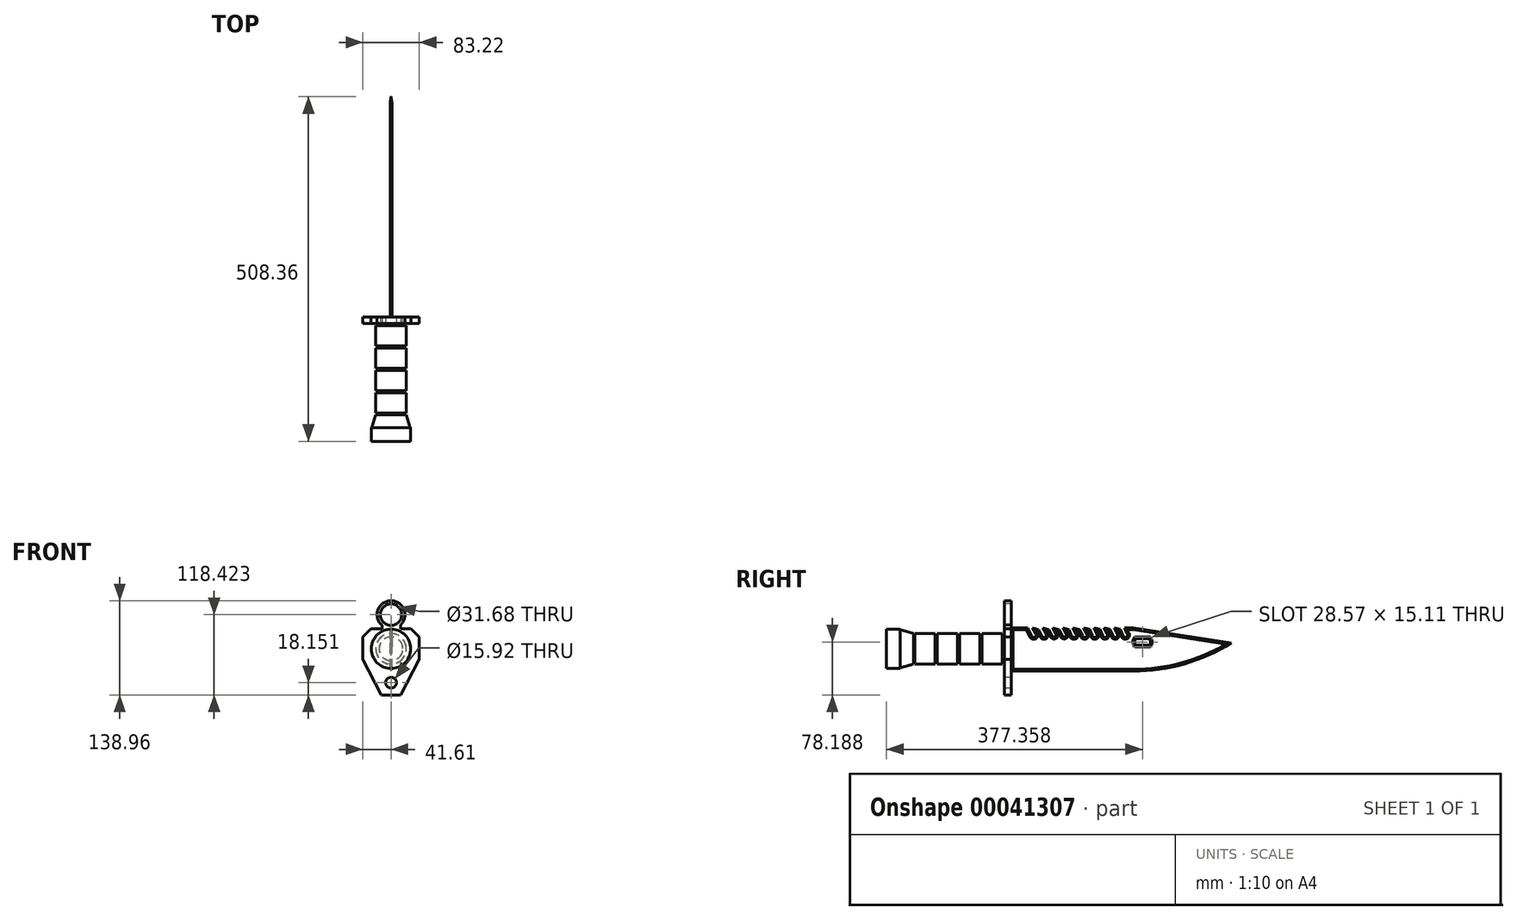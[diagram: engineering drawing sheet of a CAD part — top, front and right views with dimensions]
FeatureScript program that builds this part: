
annotation { "Feature Type Name" : "Feature", "Feature Type Description" : "" }
export const myFeature = defineFeature(function(context is Context, id is Id, definition is map)
    precondition{}
    {
        {
            var Q0;
            Q0=qCreatedBy(makeId("Right.planeOp"),FACE);
            var sketch = newSketch(context, id + "F0", { "sketchPlane" : qUnion([Q0])});
            skLineSegment(sketch, "E0", {"start": v(0, 0) * mm, "end": v(0, 17.36) * mm});
            skLineSegment(sketch, "E1", {"start": v(0, 17.36) * mm, "end": v(-3, 17.36) * mm});
            skLineSegment(sketch, "E2", {"start": v(-3, 17.36) * mm, "end": v(-3, 22.36) * mm});
            skLineSegment(sketch, "E3", {"start": v(-3, 22.36) * mm, "end": v(-33, 22.36) * mm});
            skLineSegment(sketch, "E4", {"start": v(-33, 22.36) * mm, "end": v(-33, 17.36) * mm});
            skLineSegment(sketch, "E5", {"start": v(-33, 17.36) * mm, "end": v(-36, 17.36) * mm});
            skLineSegment(sketch, "E6", {"start": v(-36, 17.36) * mm, "end": v(-36, 22.36) * mm});
            skLineSegment(sketch, "E7", {"start": v(-36, 22.36) * mm, "end": v(-66, 22.36) * mm});
            skLineSegment(sketch, "E8", {"start": v(-66, 22.36) * mm, "end": v(-66, 17.36) * mm});
            skLineSegment(sketch, "E9", {"start": v(-66, 17.36) * mm, "end": v(-69, 17.36) * mm});
            skLineSegment(sketch, "E10", {"start": v(-69, 17.36) * mm, "end": v(-69, 22.36) * mm});
            skLineSegment(sketch, "E11", {"start": v(-69, 22.36) * mm, "end": v(-99, 22.36) * mm});
            skLineSegment(sketch, "E12", {"start": v(-99, 22.36) * mm, "end": v(-99, 17.36) * mm});
            skLineSegment(sketch, "E13", {"start": v(-99, 17.36) * mm, "end": v(-102, 17.36) * mm});
            skLineSegment(sketch, "E14", {"start": v(-102, 17.36) * mm, "end": v(-102, 22.36) * mm});
            skLineSegment(sketch, "E15", {"start": v(-102, 22.36) * mm, "end": v(-132, 22.36) * mm});
            skLineSegment(sketch, "E16", {"start": v(-132, 22.36) * mm, "end": v(-132, 17.64) * mm});
            skLineSegment(sketch, "E17", {"start": v(-132, 17.64) * mm, "end": v(-134, 17.64) * mm});
            skLineSegment(sketch, "E18", {"start": v(-134, 17.64) * mm, "end": v(-134, 22.64) * mm});
            skLineSegment(sketch, "E19", {"start": v(-134, 22.64) * mm, "end": v(-153.56, 28.06) * mm});
            skLineSegment(sketch, "E20", {"start": v(-153.56, 28.06) * mm, "end": v(-153.56, 29.06) * mm});
            skLineSegment(sketch, "E21", {"start": v(-153.56, 29.06) * mm, "end": v(-173.56, 29.06) * mm});
            skLineSegment(sketch, "E22", {"start": v(-173.56, 29.06) * mm, "end": v(-173.56, 0) * mm});
            skLineSegment(sketch, "E23", {"start": v(-173.56, 0) * mm, "end": v(0, 0) * mm});
            skSolve(sketch);
        }
        {
            var Q0;
            Q0 = qSketchRegion(id + "F0", true);
            var Q1;
            Q1=sQuery(id+"F0.wireOp",EDGE,"E23");
            revolve(context, id + "F1", {"entities" : qUnion([Q0]), "axis" : qUnion([Q1]), "revolveType" : RevolveType.FULL});
        }
        {
            var Q0;
            Q0=qCreatedBy(makeId("Front.planeOp"),FACE);
            var sketch = newSketch(context, id + "F2", { "sketchPlane" : qUnion([Q0])});
            skLineSegment(sketch, "E24", {"start": v(0, -68.1) * mm, "end": v(14.11, -68.1) * mm});
            skLineSegment(sketch, "E25", {"start": v(14.11, -68.1) * mm, "end": v(41.6, -15.3) * mm});
            skLineSegment(sketch, "E26", {"start": v(41.6, -15.3) * mm, "end": v(41.6, 17.5) * mm});
            skLineSegment(sketch, "E27", {"start": v(0, 29.79) * mm, "end": v(29.7, 29.79) * mm});
            skLineSegment(sketch, "E28", {"start": v(29.7, 29.79) * mm, "end": v(41.6, 17.5) * mm});
            skLineSegment(sketch, "E29.MirrorCS", {"start": v(-41.6, -15.3) * mm, "end": v(-41.6, 17.5) * mm});
            skLineSegment(sketch, "E30.MirrorCS", {"start": v(0, 29.79) * mm, "end": v(-29.7, 29.79) * mm});
            skLineSegment(sketch, "E31.MirrorCS", {"start": v(0, -68.1) * mm, "end": v(-14.11, -68.1) * mm});
            skLineSegment(sketch, "E32.MirrorCS", {"start": v(-14.11, -68.1) * mm, "end": v(-41.6, -15.3) * mm});
            skLineSegment(sketch, "E33.MirrorCS", {"start": v(-29.7, 29.79) * mm, "end": v(-41.6, 17.5) * mm});
            skCircle(sketch, "E34", {"center": v(0, -49.95) * mm, "radius": 7.96 * mm});
            skCircle(sketch, "E35", {"center": v(0, 50.32) * mm, "radius": 20.54 * mm});
            skCircle(sketch, "E36", {"center": v(0, 50.32) * mm, "radius": 15.84 * mm});
            skLineSegment(sketch, "E37", {"start": v(14.21, 35.5) * mm, "end": v(14.21, 29.79) * mm});
            skLineSegment(sketch, "E38", {"start": v(-13.2, 29.79) * mm, "end": v(-13.2, 34.59) * mm});
            skSolve(sketch);
        }
        {
            var Q0;
            Q0 = qSketchRegion(id + "F2", true);
            extrude(context, id + "F3", {"entities" : qUnion([Q0]), "operationType" : NewBodyOperationType.ADD, "oppositeDirection" : true, "depth" : 10 * mm});
        }
        {
            var Q0;
            Q0=qCreatedBy(makeId("Right.planeOp"),FACE);
            var sketch = newSketch(context, id + "F4", { "sketchPlane" : qUnion([Q0])});
            skLineSegment(sketch, "E39", {"start": v(0, 0) * mm, "end": v(0, 30.7) * mm});
            skLineSegment(sketch, "E40", {"start": v(10.33, 30.7) * mm, "end": v(190.33, 30.7) * mm});
            skLineSegment(sketch, "E41", {"start": v(190.33, 30.7) * mm, "end": v(334.8, 8.42) * mm});
            skLineSegment(sketch, "E42", {"start": v(10.33, -32.89) * mm, "end": v(190.33, -32.89) * mm});
            skArc(sketch, "E43", {"start": v(190.33, -32.89) * mm, "mid": v(265.46, -22.36) * mm, "end": v(334.8, 8.42) * mm});
            skCircle(sketch, "E44", {"center": v(43.38, 20.17) * mm, "radius": 3.5 * mm});
            skLineSegment(sketch, "E45", {"start": v(41.53, 30.7) * mm, "end": v(47.34, 20.24) * mm});
            skLineSegment(sketch, "E46", {"start": v(34.52, 30.7) * mm, "end": v(41.24, 16.49) * mm});
            skCircle(sketch, "E47", {"center": v(58.38, 20.17) * mm, "radius": 3.5 * mm});
            skLineSegment(sketch, "E48", {"start": v(56.53, 30.7) * mm, "end": v(62.34, 20.23) * mm});
            skLineSegment(sketch, "E49", {"start": v(10.33, 30.7) * mm, "end": v(10.33, -32.89) * mm});
            skLineSegment(sketch, "E50", {"start": v(55.4, 18.32) * mm, "end": v(49.52, 30.7) * mm});
            skLineSegment(sketch, "E51", {"start": v(41.53, 30.7) * mm, "end": v(50.56, 28.52) * mm});
            skCircle(sketch, "E52", {"center": v(73.38, 20.17) * mm, "radius": 3.02 * mm});
            skLineSegment(sketch, "E53", {"start": v(64.52, 30.7) * mm, "end": v(71.98, 16.29) * mm});
            skLineSegment(sketch, "E54", {"start": v(71.53, 30.7) * mm, "end": v(77.13, 19.4) * mm});
            skLineSegment(sketch, "E55", {"start": v(56.53, 30.7) * mm, "end": v(65.66, 28.52) * mm});
            skCircle(sketch, "E56", {"center": v(88.38, 20.17) * mm, "radius": 3 * mm});
            skLineSegment(sketch, "E57", {"start": v(85.71, 18.8) * mm, "end": v(79.52, 30.7) * mm});
            skLineSegment(sketch, "E58", {"start": v(64.52, 30.7) * mm, "end": v(79.52, 30.7) * mm});
            skLineSegment(sketch, "E59", {"start": v(71.53, 30.7) * mm, "end": v(80.66, 28.52) * mm});
            skLineSegment(sketch, "E60", {"start": v(91.21, 21.13) * mm, "end": v(86.53, 30.7) * mm});
            skCircle(sketch, "E61", {"center": v(102.57, 20.17) * mm, "radius": 3.5 * mm});
            skLineSegment(sketch, "E62", {"start": v(99.3, 18.91) * mm, "end": v(94.77, 30.7) * mm});
            skLineSegment(sketch, "E63", {"start": v(106.07, 20.24) * mm, "end": v(101.13, 30.7) * mm});
            skLineSegment(sketch, "E64", {"start": v(86.53, 30.7) * mm, "end": v(95.61, 28.52) * mm});
            skCircle(sketch, "E65", {"center": v(118.43, 20.17) * mm, "radius": 3.5 * mm});
            skLineSegment(sketch, "E66", {"start": v(114.93, 20.24) * mm, "end": v(109.99, 30.7) * mm});
            skLineSegment(sketch, "E67", {"start": v(109.99, 30.7) * mm, "end": v(101.13, 30.7) * mm});
            skLineSegment(sketch, "E68", {"start": v(111.02, 28.52) * mm, "end": v(101.13, 30.7) * mm});
            skLineSegment(sketch, "E69", {"start": v(121.93, 20.24) * mm, "end": v(116.98, 30.7) * mm});
            skCircle(sketch, "E70", {"center": v(133.43, 20.17) * mm, "radius": 3.5 * mm});
            skLineSegment(sketch, "E71", {"start": v(129.93, 20.24) * mm, "end": v(124.99, 30.7) * mm});
            skLineSegment(sketch, "E72", {"start": v(124.99, 30.7) * mm, "end": v(132.31, 30.7) * mm});
            skLineSegment(sketch, "E73", {"start": v(136.93, 20.24) * mm, "end": v(131.98, 30.7) * mm});
            skLineSegment(sketch, "E74", {"start": v(116.98, 30.7) * mm, "end": v(125.92, 28.73) * mm});
            skCircle(sketch, "E75", {"center": v(148.43, 20.24) * mm, "radius": 3.5 * mm});
            skLineSegment(sketch, "E76", {"start": v(144.93, 20.17) * mm, "end": v(139.95, 30.7) * mm});
            skLineSegment(sketch, "E77", {"start": v(140.88, 28.73) * mm, "end": v(132.31, 30.7) * mm});
            skLineSegment(sketch, "E78", {"start": v(151.93, 20.24) * mm, "end": v(146.99, 30.7) * mm});
            skCircle(sketch, "E79", {"center": v(163.43, 20.24) * mm, "radius": 3.5 * mm});
            skLineSegment(sketch, "E80", {"start": v(159.93, 20.17) * mm, "end": v(154.95, 30.7) * mm});
            skLineSegment(sketch, "E81", {"start": v(166.93, 20.24) * mm, "end": v(161.99, 30.7) * mm});
            skCircle(sketch, "E82", {"center": v(178.43, 20.24) * mm, "radius": 3.5 * mm});
            skLineSegment(sketch, "E83", {"start": v(174.93, 20.24) * mm, "end": v(169.99, 30.7) * mm});
            skLineSegment(sketch, "E84", {"start": v(181.93, 20.24) * mm, "end": v(176.99, 30.7) * mm});
            skLineSegment(sketch, "E85", {"start": v(161.99, 30.7) * mm, "end": v(170.96, 28.64) * mm});
            skLineSegment(sketch, "E86", {"start": v(146.99, 30.7) * mm, "end": v(155.92, 28.64) * mm});
            skLineSegment(sketch, "E87", {"start": v(193.78, 14.96) * mm, "end": v(213.63, 14.96) * mm});
            skLineSegment(sketch, "E88", {"start": v(193.78, 5.21) * mm, "end": v(213.63, 5.21) * mm});
            skArc(sketch, "E89", {"start": v(193.78, 14.96) * mm, "mid": v(192.2, 10.09) * mm, "end": v(193.78, 5.21) * mm});
            skArc(sketch, "E90", {"start": v(213.63, 5.21) * mm, "mid": v(215.4, 10.09) * mm, "end": v(213.63, 14.96) * mm});
            skSolve(sketch);
        }
        {
            var Q0;
            {var subQ66=sQuery(id+"F4.wireOp",EDGE,"E41");Q0=makeQuery(id+"F4.imprint","IMPRINT",FACE,{"disambiguationData":[TD([[makeQuery(id+"F4.imprint","IMPRINT",EDGE,{"derivedFrom":subQ66}),-1.0]])]});}
            extrude(context, id + "F5", {"entities" : qUnion([Q0]), "endBound" : BoundingType.SYMMETRIC, "depth" : 2.5 * mm, "hasDraft" : true, "draftAngle" : 65 * degree, "draftPullDirection" : true});
        }
    });
